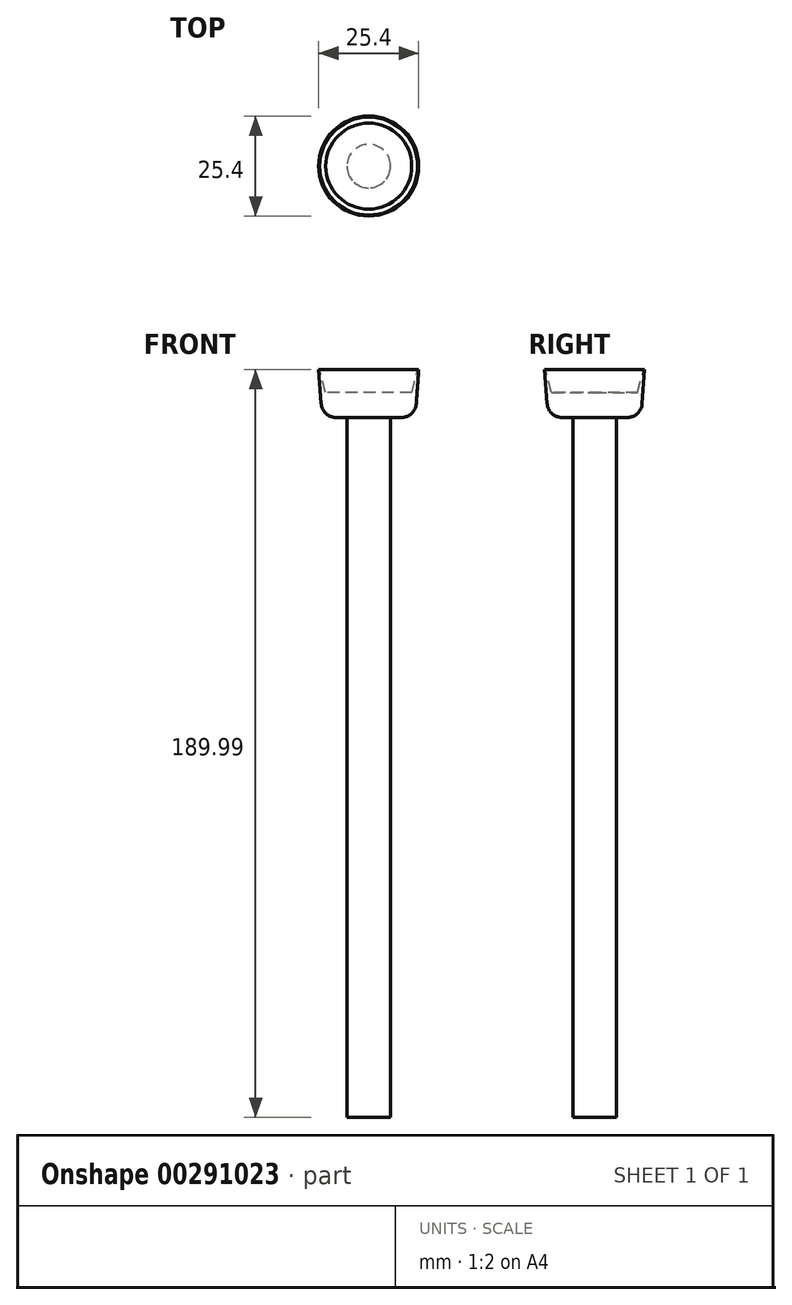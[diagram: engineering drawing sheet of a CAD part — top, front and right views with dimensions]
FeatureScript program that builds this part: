
annotation { "Feature Type Name" : "Feature", "Feature Type Description" : "" }
export const myFeature = defineFeature(function(context is Context, id is Id, definition is map)
    precondition{}
    {
        {
            var Q0;
            Q0=qCreatedBy(makeId("Front.planeOp"),FACE);
            var sketch = newSketch(context, id + "F0", { "sketchPlane" : qUnion([Q0])});
            skLineSegment(sketch, "E0", {"start": v(0, 0) * mm, "end": v(11.81, 0) * mm});
            skLineSegment(sketch, "E1", {"start": v(11.81, 0) * mm, "end": v(12.7, 12.2) * mm});
            skLineSegment(sketch, "E2", {"start": v(10.92, 6.35) * mm, "end": v(0, 6.35) * mm});
            skLineSegment(sketch, "E3", {"start": v(0, 6.35) * mm, "end": v(0, 0) * mm});
            skLineSegment(sketch, "E4", {"start": v(12.7, 12.2) * mm, "end": v(12.45, 12.2) * mm});
            skLineSegment(sketch, "E5", {"start": v(12.45, 12.2) * mm, "end": v(10.92, 6.35) * mm});
            skSolve(sketch);
        }
        {
            var Q0;
            Q0=makeQuery(id+"F0.imprint","IMPRINT",FACE,{"disambiguationData":[TD([[makeQuery(id+"F0.imprint","IMPRINT",EDGE,{"derivedFrom":sQuery(id+"F0.wireOp",EDGE,"E0")}),1.0]])]});
            var Q1;
            Q1=sQuery(id+"F0.wireOp",EDGE,"E3");
            revolve(context, id + "F1", {"entities" : qUnion([Q0]), "axis" : qUnion([Q1]), "revolveType" : RevolveType.FULL});
        }
        {
            var Q0;
            Q0=makeQuery(id+"F1.opRevolve","SWEPT_EDGE",EDGE,{"disambiguationData":[OSD([sQuery(id+"F0.wireOp",EDGE,"E0"),sQuery(id+"F0.wireOp",EDGE,"E1")])]});
            fillet(context, id + "F2", {"entities" : qUnion([Q0]), "radius" : 3.8 * mm, "tangentPropagation" : true, "allowEdgeOverflow" : false});
        }
        {
            var Q0;
            Q0=makeQuery(id+"F1.opRevolve","SWEPT_FACE",FACE,{"disambiguationData":[OSD([sQuery(id+"F0.wireOp",EDGE,"E0")])]});
            var sketch = newSketch(context, id + "F3", { "sketchPlane" : qUnion([Q0])});
            skCircle(sketch, "E6", {"center": v(0, 0) * mm, "radius": 5.54 * mm});
            skSolve(sketch);
        }
        {
            var Q0;
            Q0 = qSketchRegion(id + "F3", true);
            extrude(context, id + "F4", {"entities" : qUnion([Q0]), "operationType" : NewBodyOperationType.ADD, "depth" : 177.8 * mm});
        }
    });
